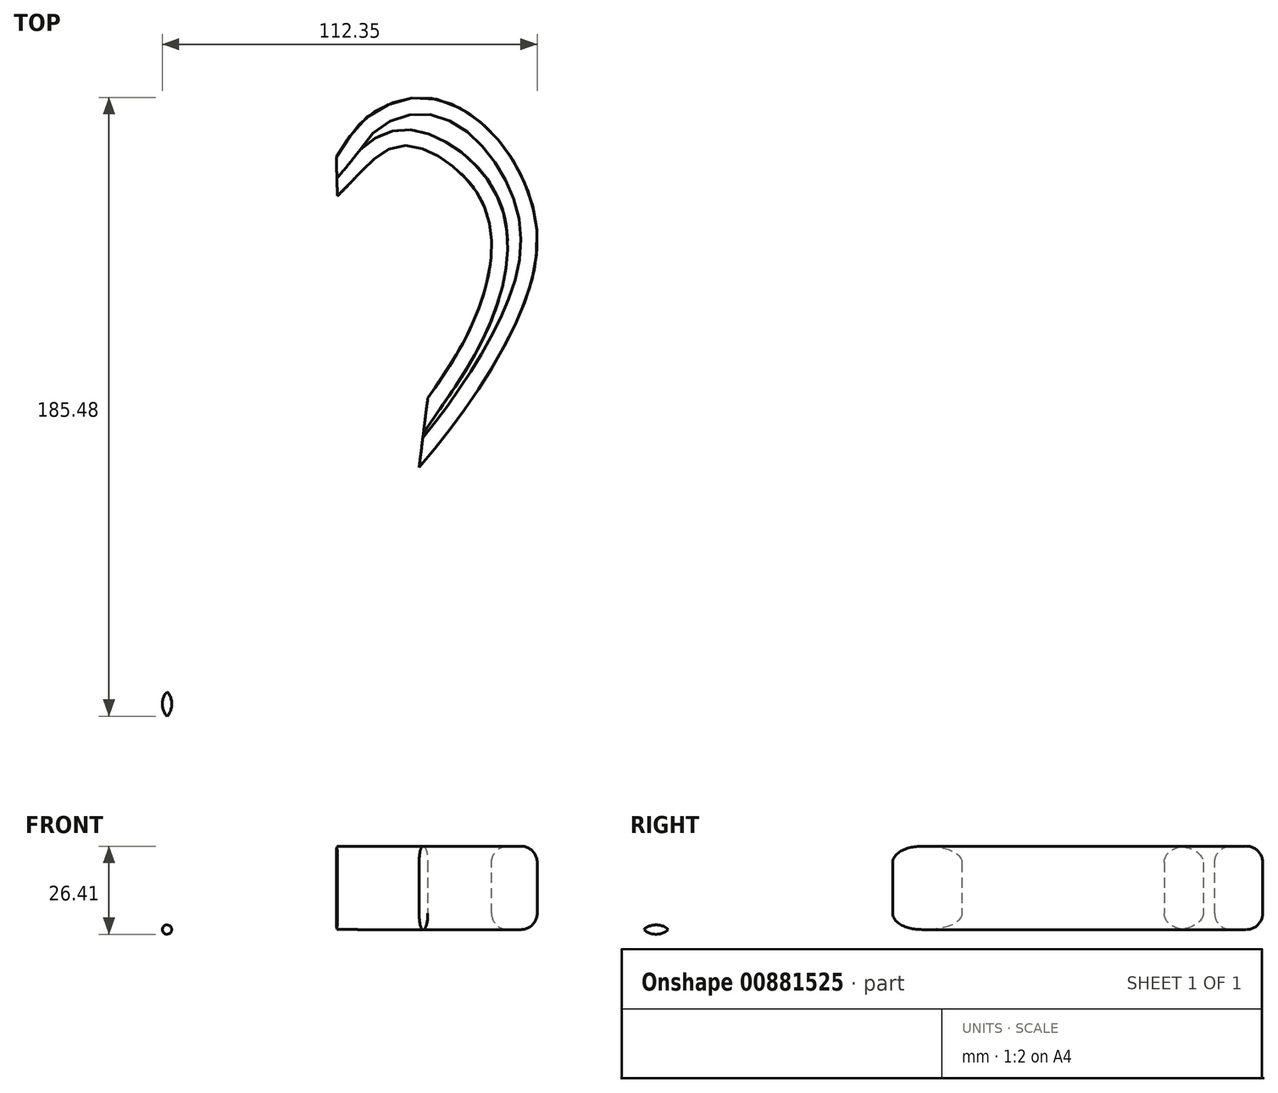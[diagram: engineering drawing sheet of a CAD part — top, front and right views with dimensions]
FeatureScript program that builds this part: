
annotation { "Feature Type Name" : "Feature", "Feature Type Description" : "" }
export const myFeature = defineFeature(function(context is Context, id is Id, definition is map)
    precondition{}
    {
        {
            var Q0;
            Q0=qCreatedBy(makeId("Top.planeOp"),FACE);
            var sketch = newSketch(context, id + "F0", { "sketchPlane" : qUnion([Q0])});
            skLineSegment(sketch, "E0", {"start": v(-27.86, 104.76) * mm, "end": v(-27.86, -100.24) * mm});
            skFitSpline(sketch, "E1", {"points": [v(31, 104.76) * mm, v(32.15, 96.06) * mm, v(32.43, 92.62) * mm, v(22.12, 84.31) * mm, v(7.52, 64.55) * mm, v(2.07, 40.78) * mm, v(6.37, 8.7) * mm, v(19.83, -28.24) * mm, v(27.23, -52.25) * mm, v(22.16, -58.48) * mm, v(27.84, -63.45) * mm, v(60.67, -63.42) * mm, v(82.64, -63.46) * mm, v(82.64, -56.22) * mm, v(65.49, -56.6) * mm, v(43.89, -56.3) * mm, v(34.14, -56.16) * mm, v(34.14, -46.37) * mm, v(15.58, 0) * mm, v(8.12, 36.03) * mm, v(14.1, 66.23) * mm, v(35.83, 87.62) * mm, v(41.02, 90.62) * mm, v(36.23, 104.76) * mm, v(31, 104.76) * mm]});
            skLineSegment(sketch, "E2", {"start": v(82.64, 104.76) * mm, "end": v(82.64, -63.46) * mm});
            skSolve(sketch);
        }
        {
            var Q0;
            {var subQ0=sQuery(id+"F0.wireOp",EDGE,"E2");var subQ1=sQuery(id+"F0.wireOp",EDGE,"E1");var subQ2=makeQuery(id+"F0.imprint","INTERSECT",VERTEX,{"disambiguationData":[OD(0.0)],"derivedFrom":[subQ1,subQ0]});Q0=makeQuery(id+"F0.imprint","IMPRINT",FACE,{"disambiguationData":[TD([[makeQuery(id+"F0.imprint","IMPRINT",EDGE,{"disambiguationData":[TD([[subQ2,1.0]])],"derivedFrom":subQ1}),1.0]])]});}
            var Q1;
            Q1=sQuery(id+"F0.wireOp",EDGE,"E2");
            revolve(context, id + "F1", {"surfaceOperationType" : NewSurfaceOperationType.NEW, "entities" : qUnion([Q0]), "axis" : qUnion([Q1]), "revolveType" : RevolveType.FULL});
        }
        {
            var Q0;
            Q0=qCreatedBy(makeId("Top.planeOp"),FACE);
            var sketch = newSketch(context, id + "F2", { "sketchPlane" : qUnion([Q0])});
            skFitSpline(sketch, "E3", {"points": [v(158.2, 11.1) * mm, v(174.42, 32.18) * mm, v(192.58, 69.8) * mm, v(189.99, 96.07) * mm, v(176.37, 114.88) * mm, v(158.53, 122.02) * mm, v(141.8, 115.55) * mm, v(133.38, 104.2) * mm], "startDerivative": vector(105.04, 125.99) * mm, "endDerivative": vector(-80.5, -116.23) * mm});
            skFitSpline(sketch, "E4", {"points": [v(160.8, 31.86) * mm, v(173.45, 52.61) * mm, v(179.93, 77.9) * mm, v(173.45, 96.4) * mm, v(157.88, 107.1) * mm, v(147.65, 105.82) * mm, v(133.7, 92.53) * mm], "startDerivative": vector(73.02, 105.85) * mm, "endDerivative": vector(-104.18, -99.4) * mm});
            skLineSegment(sketch, "E5", {"start": v(133.38, 104.2) * mm, "end": v(133.7, 92.53) * mm});
            skLineSegment(sketch, "E6", {"start": v(160.8, 31.86) * mm, "end": v(158.2, 11.1) * mm});
            skSolve(sketch);
        }
        {
            var Q0;
            Q0=makeQuery(id+"F2.imprint","IMPRINT",FACE,{"disambiguationData":[TD([[makeQuery(id+"F2.imprint","IMPRINT",EDGE,{"derivedFrom":sQuery(id+"F2.wireOp",EDGE,"E3")}),1.0]])]});
            extrude(context, id + "F3", {"entities" : qUnion([Q0]), "depth" : 25 * mm, "offsetDistance" : 25 * mm});
        }
        {
            var Q0;
            Q0=makeQuery(id+"F3.opExtrude","CAP_EDGE",EDGE,{"disambiguationData":[OSD([sQuery(id+"F2.wireOp",EDGE,"E3")])],"isStart":false});
            var Q1;
            Q1=makeQuery(id+"F3.opExtrude","CAP_EDGE",EDGE,{"disambiguationData":[OSD([sQuery(id+"F2.wireOp",EDGE,"E3")])],"isStart":true});
            var Q2;
            Q2=makeQuery(id+"F3.opExtrude","CAP_EDGE",EDGE,{"disambiguationData":[OSD([sQuery(id+"F2.wireOp",EDGE,"E4")])],"isStart":false});
            var Q3;
            Q3=makeQuery(id+"F3.opExtrude","CAP_EDGE",EDGE,{"disambiguationData":[OSD([sQuery(id+"F2.wireOp",EDGE,"E4")])],"isStart":true});
            fillet(context, id + "F4", {"entities" : qUnion([Q0, Q1, Q2, Q3]), "radius" : 4.83 * mm, "tangentPropagation" : true, "allowEdgeOverflow" : false});
        }
    });
